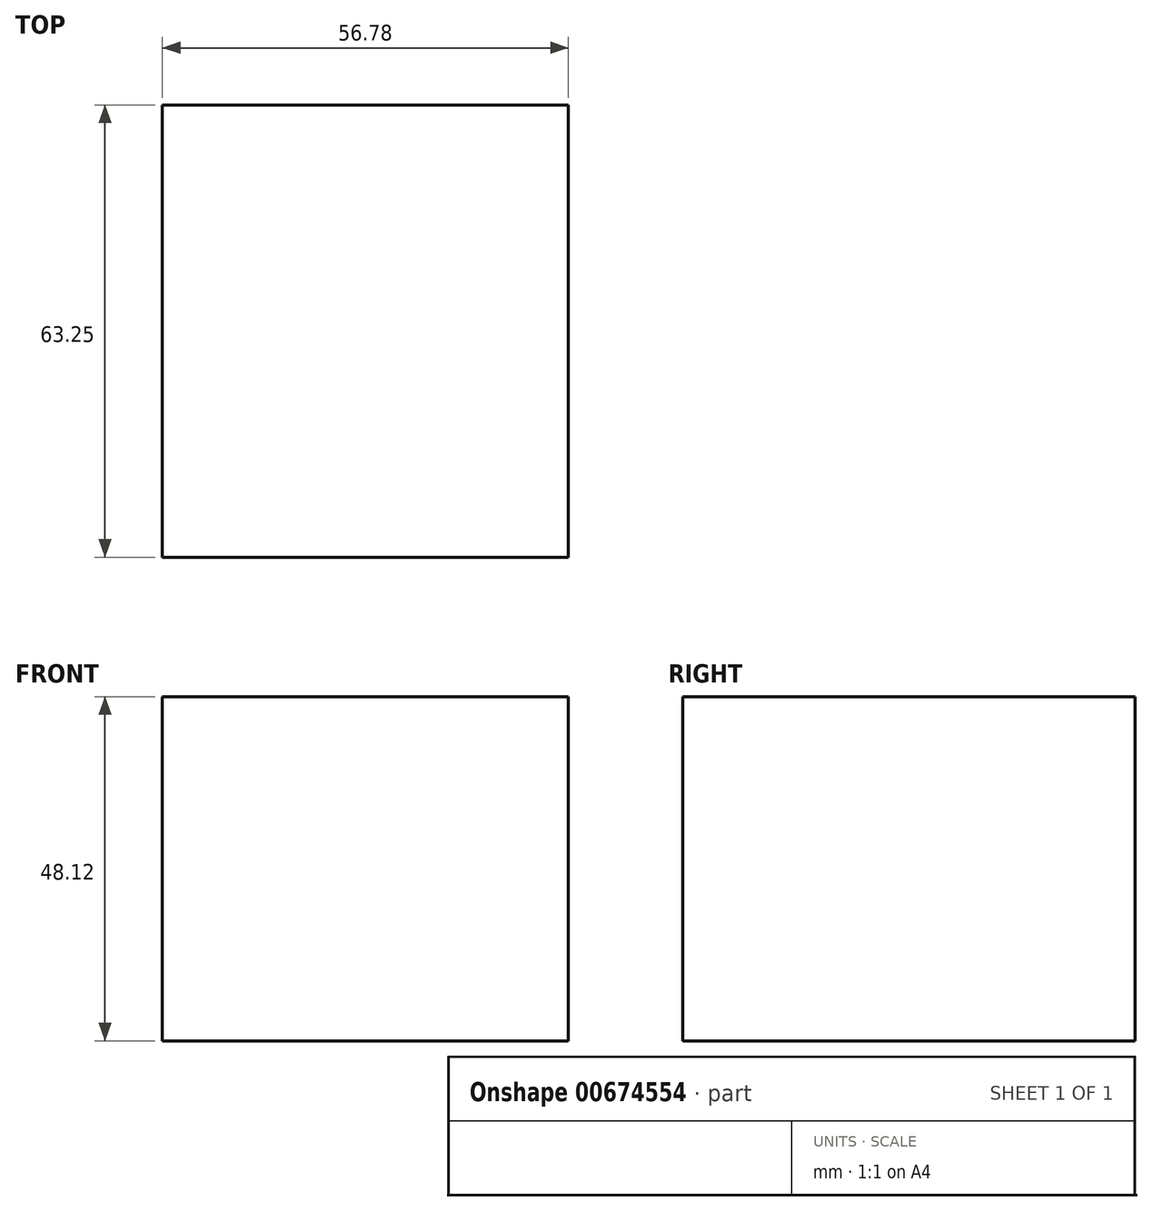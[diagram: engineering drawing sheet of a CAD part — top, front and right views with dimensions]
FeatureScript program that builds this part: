
annotation { "Feature Type Name" : "Feature", "Feature Type Description" : "" }
export const myFeature = defineFeature(function(context is Context, id is Id, definition is map)
    precondition{}
    {
        {
            var Q0;
            Q0=qCreatedBy(makeId("Front.planeOp"),FACE);
            var sketch = newSketch(context, id + "F0", { "sketchPlane" : qUnion([Q0])});
            skLineSegment(sketch, "E0.bottom", {"start": v(21.48, 25.72) * mm, "end": v(-35.3, 25.72) * mm});
            skLineSegment(sketch, "E0.top", {"start": v(21.48, -22.4) * mm, "end": v(-35.3, -22.4) * mm});
            skLineSegment(sketch, "E0.left", {"start": v(21.48, 25.72) * mm, "end": v(21.48, -22.4) * mm});
            skLineSegment(sketch, "E0.right", {"start": v(-35.3, 25.72) * mm, "end": v(-35.3, -22.4) * mm});
            skSolve(sketch);
        }
        {
            var Q0;
            Q0 = qSketchRegion(id + "F0", true);
            extrude(context, id + "F1", {"entities" : qUnion([Q0]), "depth" : 63.25 * mm, "offsetDistance" : 25.4 * mm});
        }
    });
